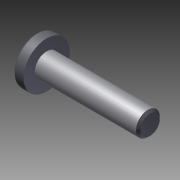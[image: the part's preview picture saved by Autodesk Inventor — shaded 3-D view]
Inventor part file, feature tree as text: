
AUTODESK INVENTOR PART (.ipt)
format: ipt  version: 2015 (Build 190159000, 159)  size: 127,488 bytes
history: native  units: in
note: dims shown in document units (in); Inventor stores cm internally (conversion verified against a paired STEP export)
features: chamfer x1, other x1, imported_body x1
ambient origin geometry x8: Origin, YZ Plane, XZ Plane, XY Plane, X Axis, Y Axis, Z Axis, Center Point
bodies: Body1 (feature_tree)
feature tree (3):
  chamfer  "Chamfer1"  [1 undecoded]
  other  "2-56 X 0.375 PHS (PHS-09)1"
  imported_body  "Base1"
note: 1 required parameter value undecoded (feature->parameter linkage not recoverable at this tier; creation-order binding heuristic only, values carry confidence <= 0.55)
